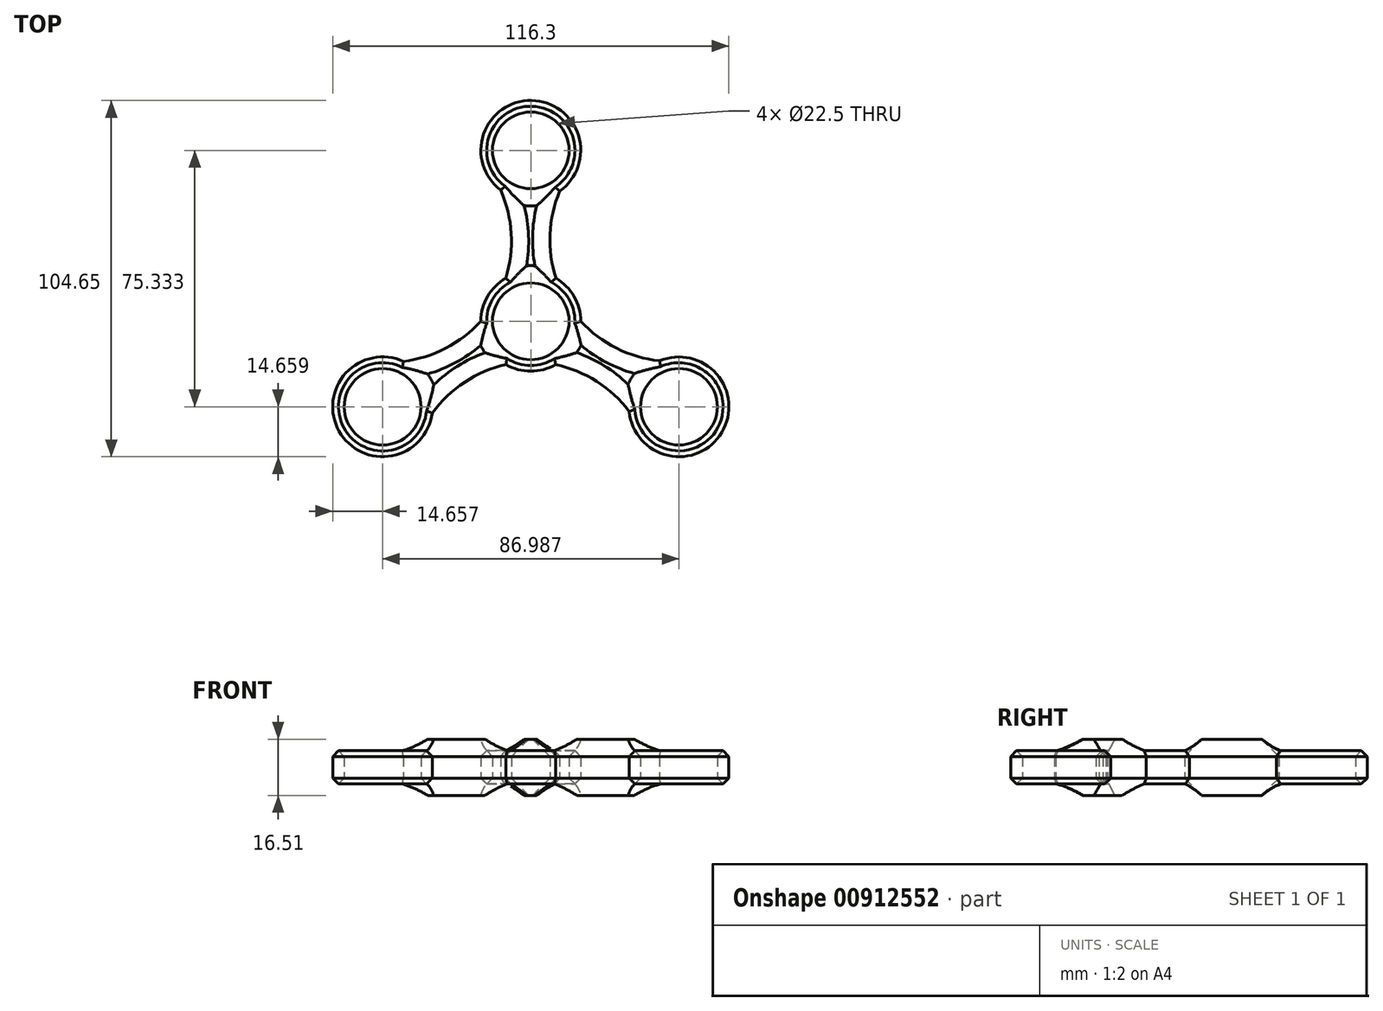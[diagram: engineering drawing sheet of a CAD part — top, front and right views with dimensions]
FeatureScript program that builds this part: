
annotation { "Feature Type Name" : "Feature", "Feature Type Description" : "" }
export const myFeature = defineFeature(function(context is Context, id is Id, definition is map)
    precondition{}
    {
        {
            var Q0;
            Q0=qCreatedBy(makeId("Top.planeOp"),FACE);
            var sketch = newSketch(context, id + "F0", { "sketchPlane" : qUnion([Q0])});
            skCircle(sketch, "E0", {"center": v(0, 0) * mm, "radius": 11.25 * mm});
            skCircle(sketch, "E1", {"center": v(0, 50.22) * mm, "radius": 11.25 * mm});
            skArc(sketch, "E2", {"start": v(-7.37, 12.67) * mm, "mid": v(0, -14.66) * mm, "end": v(7.37, 12.67) * mm});
            skArc(sketch, "E3", {"start": v(8.5, 38.28) * mm, "mid": v(0.23, 64.88) * mm, "end": v(-8.87, 38.55) * mm});
            skArc(sketch, "E4", {"start": v(-7.37, 12.67) * mm, "mid": v(-5.76, 25.74) * mm, "end": v(-8.87, 38.55) * mm});
            skArc(sketch, "E5", {"start": v(8.5, 38.28) * mm, "mid": v(5.63, 25.57) * mm, "end": v(7.37, 12.67) * mm});
            skCircle(sketch, "E6.1.0", {"center": v(-43.5, -25.11) * mm, "radius": 11.25 * mm});
            skArc(sketch, "E6.1.1", {"start": v(-37.4, -11.78) * mm, "mid": v(-56.3, -32.24) * mm, "end": v(-28.95, -26.95) * mm});
            skArc(sketch, "E6.1.2", {"start": v(-7.29, -12.72) * mm, "mid": v(-19.42, -17.86) * mm, "end": v(-28.95, -26.95) * mm});
            skArc(sketch, "E6.1.3", {"start": v(-37.4, -11.78) * mm, "mid": v(-24.96, -7.91) * mm, "end": v(-14.66, 0.05) * mm});
            skCircle(sketch, "E6.2.0", {"center": v(43.5, -25.11) * mm, "radius": 11.25 * mm});
            skArc(sketch, "E6.2.1", {"start": v(28.9, -26.5) * mm, "mid": v(56.07, -32.64) * mm, "end": v(37.82, -11.6) * mm});
            skArc(sketch, "E6.2.2", {"start": v(14.66, 0.05) * mm, "mid": v(25.17, -7.89) * mm, "end": v(37.82, -11.6) * mm});
            skArc(sketch, "E6.2.3", {"start": v(28.9, -26.5) * mm, "mid": v(19.33, -17.66) * mm, "end": v(7.29, -12.72) * mm});
            skSolve(sketch);
        }
        {
            var Q0;
            Q0=makeQuery(id+"F0.imprint","IMPRINT",FACE,{"disambiguationData":[TD([[makeQuery(id+"F0.imprint","IMPRINT",EDGE,{"derivedFrom":sQuery(id+"F0.wireOp",EDGE,"E0")}),-1.0]])]});
            var Q1;
            Q1=makeQuery(id+"F0.imprint","IMPRINT",FACE,{"disambiguationData":[TD([[makeQuery(id+"F0.imprint","IMPRINT",EDGE,{"derivedFrom":sQuery(id+"F0.wireOp",EDGE,"E6.1.0")}),-1.0]])]});
            var Q2;
            Q2=makeQuery(id+"F0.imprint","IMPRINT",FACE,{"disambiguationData":[TD([[makeQuery(id+"F0.imprint","IMPRINT",EDGE,{"derivedFrom":sQuery(id+"F0.wireOp",EDGE,"E6.2.0")}),-1.0]])]});
            var Q3;
            Q3=makeQuery(id+"F0.imprint","IMPRINT",FACE,{"disambiguationData":[TD([[makeQuery(id+"F0.imprint","IMPRINT",EDGE,{"derivedFrom":sQuery(id+"F0.wireOp",EDGE,"4a7753a6-fd8f-44a9-b7dd-b16848ef7f71.1.3.0")}),-1.0]])]});
            extrude(context, id + "F1", {"entities" : qUnion([Q0, Q1, Q2, Q3]), "depth" : 16.5 * mm, "offsetDistance" : 25.4 * mm});
        }
        {
            var Q0;
            Q0=makeQuery(id+"F1.opExtrude","CAP_FACE",FACE,{"disambiguationData":[OSD([sQuery(id+"F0.wireOp",EDGE,"E0"),sQuery(id+"F0.wireOp",EDGE,"E1"),sQuery(id+"F0.wireOp",EDGE,"E2"),sQuery(id+"F0.wireOp",EDGE,"E3"),sQuery(id+"F0.wireOp",EDGE,"E4"),sQuery(id+"F0.wireOp",EDGE,"E5"),sQuery(id+"F0.wireOp",EDGE,"E6.1.0"),sQuery(id+"F0.wireOp",EDGE,"E6.1.1"),sQuery(id+"F0.wireOp",EDGE,"E6.1.2"),sQuery(id+"F0.wireOp",EDGE,"E6.1.3"),sQuery(id+"F0.wireOp",EDGE,"E6.2.0"),sQuery(id+"F0.wireOp",EDGE,"E6.2.1"),sQuery(id+"F0.wireOp",EDGE,"E6.2.2"),sQuery(id+"F0.wireOp",EDGE,"E6.2.3")])],"isStart":false});
            chamfer(context, id + "F2", {"entities" : qUnion([Q0]), "width" : 5.08 * mm, "tangentPropagation" : true});
        }
        {
            var Q0;
            Q0=makeQuery(id+"F1.opExtrude","CAP_FACE",FACE,{"disambiguationData":[OSD([sQuery(id+"F0.wireOp",EDGE,"E0"),sQuery(id+"F0.wireOp",EDGE,"E1"),sQuery(id+"F0.wireOp",EDGE,"E2"),sQuery(id+"F0.wireOp",EDGE,"E3"),sQuery(id+"F0.wireOp",EDGE,"E4"),sQuery(id+"F0.wireOp",EDGE,"E5"),sQuery(id+"F0.wireOp",EDGE,"E6.1.0"),sQuery(id+"F0.wireOp",EDGE,"E6.1.1"),sQuery(id+"F0.wireOp",EDGE,"E6.1.2"),sQuery(id+"F0.wireOp",EDGE,"E6.1.3"),sQuery(id+"F0.wireOp",EDGE,"E6.2.0"),sQuery(id+"F0.wireOp",EDGE,"E6.2.1"),sQuery(id+"F0.wireOp",EDGE,"E6.2.2"),sQuery(id+"F0.wireOp",EDGE,"E6.2.3")])],"isStart":true});
            chamfer(context, id + "F3", {"entities" : qUnion([Q0]), "width" : 5.08 * mm, "tangentPropagation" : true});
        }
    });
